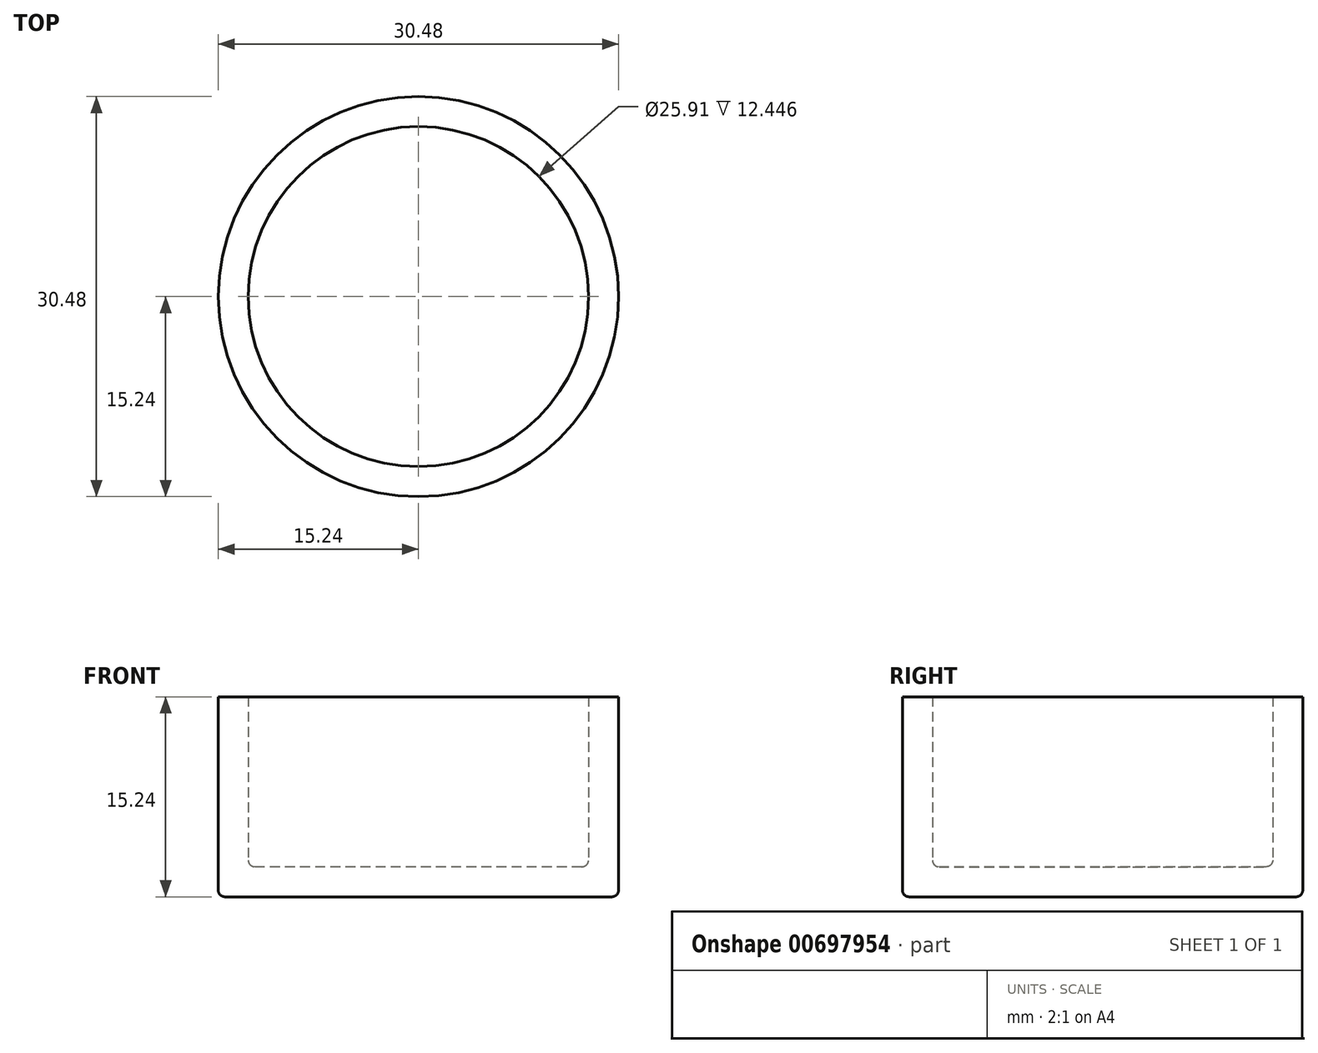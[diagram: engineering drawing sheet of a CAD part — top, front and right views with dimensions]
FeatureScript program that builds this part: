
annotation { "Feature Type Name" : "Feature", "Feature Type Description" : "" }
export const myFeature = defineFeature(function(context is Context, id is Id, definition is map)
    precondition{}
    {
        {
            var Q0;
            Q0=qCreatedBy(makeId("Top.planeOp"),FACE);
            var sketch = newSketch(context, id + "F0", { "sketchPlane" : qUnion([Q0])});
            skCircle(sketch, "E0", {"center": v(0, 0) * mm, "radius": 15.24 * mm});
            skSolve(sketch);
        }
        {
            var Q0;
            Q0 = qSketchRegion(id + "F0", true);
            var Q1;
            Q1=makeQuery(id+"F0.imprint","IMPRINT",FACE,{"disambiguationData":[TD([[makeQuery(id+"F0.imprint","IMPRINT",EDGE,{"derivedFrom":sQuery(id+"F0.wireOp",EDGE,"E0")}),1.0]])]});
            extrude(context, id + "F1", {"entities" : qUnion([Q0, Q1]), "depth" : 15.24 * mm, "offsetDistance" : 25.4 * mm});
        }
        {
            var Q0;
            Q0=makeQuery(id+"F1.opExtrude","CAP_FACE",FACE,{"disambiguationData":[OSD([sQuery(id+"F0.wireOp",EDGE,"E0")])],"isStart":false});
            shell(context, id + "F2", {"entities" : qUnion([Q0]), "thickness" : 2.3 * mm});
        }
        {
            var Q0;
            {var subQ0=sQuery(id+"F0.wireOp",EDGE,"E0");Q0=makeQuery(id+"F2.opShell","OFFSET_EDGE",EDGE,{"disambiguationData":[OSD([subQ0]),TDD([makeQuery(id+"F1.opExtrude","CAP_EDGE",EDGE,{"disambiguationData":[OSD([subQ0])],"isStart":true})])]});}
            fillet(context, id + "F3", {"entities" : qUnion([Q0]), "radius" : 0.5 * mm, "tangentPropagation" : true, "allowEdgeOverflow" : false});
        }
        {
            var Q0;
            Q0=makeQuery(id+"F1.opExtrude","CAP_EDGE",EDGE,{"disambiguationData":[OSD([sQuery(id+"F0.wireOp",EDGE,"E0")])],"isStart":true});
            fillet(context, id + "F4", {"entities" : qUnion([Q0]), "radius" : 0.5 * mm, "tangentPropagation" : true, "allowEdgeOverflow" : false});
        }
    });
